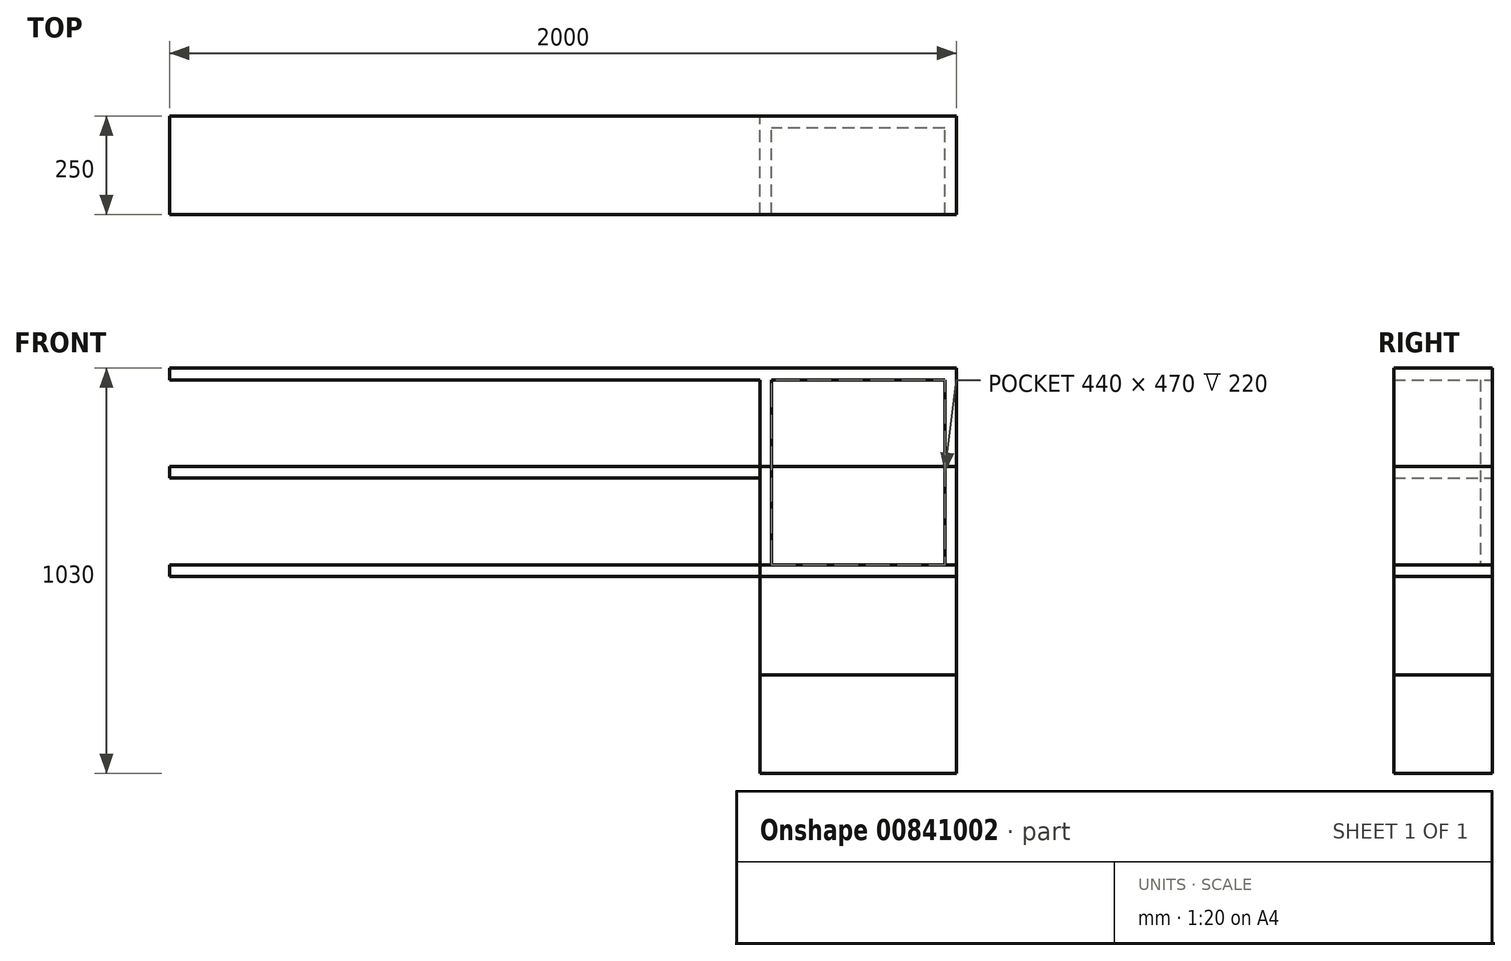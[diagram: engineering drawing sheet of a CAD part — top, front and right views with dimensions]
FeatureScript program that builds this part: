
annotation { "Feature Type Name" : "Feature", "Feature Type Description" : "" }
export const myFeature = defineFeature(function(context is Context, id is Id, definition is map)
    precondition{}
    {
        {
            var Q0;
            Q0=qCreatedBy(makeId("Top.planeOp"),FACE);
            var sketch = newSketch(context, id + "F0", { "sketchPlane" : qUnion([Q0])});
            skLineSegment(sketch, "E0.bottom", {"start": v(750, -125) * mm, "end": v(-750, -125) * mm});
            skLineSegment(sketch, "E0.top", {"start": v(750, 125) * mm, "end": v(-750, 125) * mm});
            skLineSegment(sketch, "E0.left", {"start": v(750, -125) * mm, "end": v(750, 125) * mm});
            skLineSegment(sketch, "E0.right", {"start": v(-750, -125) * mm, "end": v(-750, 125) * mm});
            skPoint(sketch, "E0.middle", {"position": v(0, 0) * mm});
            skSolve(sketch);
        }
        {
            var Q0;
            Q0=qSketchRegion(id+"F0",true);
            extrude(context, id + "F1", {"entities" : qUnion([Q0]), "depth" : 30 * mm, "offsetDistance" : 25 * mm});
        }
        {
            var Q0;
            Q0=makeQuery(id+"F1.opExtrude","SWEPT_FACE",FACE,{"disambiguationData":[OSD([sQuery(id+"F0.wireOp",EDGE,"E0.left")])]});
            extrude(context, id + "F2", {"entities" : qUnion([Q0]), "depth" : 500 * mm, "offsetDistance" : 25 * mm});
        }
        {
            var Q0;
            {var subQ0=sQuery(id+"F0.wireOp",EDGE,"E0.left");Q0=makeQuery(id+"F2.opExtrude","SWEPT_FACE",FACE,{"disambiguationData":[OSD([subQ0]),TDD([makeQuery(id+"F1.opExtrude","CAP_EDGE",EDGE,{"disambiguationData":[OSD([subQ0])],"isStart":true})])]});}
            extrude(context, id + "F3", {"entities" : qUnion([Q0]), "operationType" : NewBodyOperationType.ADD, "depth" : 500 * mm, "offsetDistance" : 25 * mm});
        }
        {
            var Q0;
            Q0=makeQuery(id+"F1.opExtrude","SWEPT_BODY",BODY,{"disambiguationData":[OSD([sQuery(id+"F0.wireOp",EDGE,"E0.bottom"),sQuery(id+"F0.wireOp",EDGE,"E0.top"),sQuery(id+"F0.wireOp",EDGE,"E0.left"),sQuery(id+"F0.wireOp",EDGE,"E0.right")])]});
            transform(context, id + "F4", {"entities" : qUnion([Q0]), "transformType" : TransformType.TRANSLATION_3D, "dx" : 0 * mm, "dy" : 0 * mm, "dz" : 0 * mm, "makeCopy" : true});
        }
        {
            var Q0;
            {var subQ0=sQuery(id+"F0.wireOp",EDGE,"E0.left");var subQ1=sQuery(id+"F0.wireOp",EDGE,"E0.bottom");Q0=makeQuery(id+"F3.boolean.opBoolean","MERGE",FACE,{"derivedFrom":[makeQuery(id+"F2.opExtrude","SWEPT_FACE",FACE,{"disambiguationData":[OSD([subQ1,subQ0])]}),makeQuery(id+"F3.opExtrude","SWEPT_FACE",FACE,{"disambiguationData":[OSD([subQ1,subQ0])]})]});}
            shell(context, id + "F5", {"entities" : qUnion([Q0]), "thickness" : 30 * mm});
        }
        {
            var Q0;
            Q0=makeQuery(id+"F4.opPattern","COPY",BODY,{"derivedFrom":makeQuery(id+"F1.opExtrude","SWEPT_BODY",BODY,{"disambiguationData":[OSD([sQuery(id+"F0.wireOp",EDGE,"E0.bottom"),sQuery(id+"F0.wireOp",EDGE,"E0.top"),sQuery(id+"F0.wireOp",EDGE,"E0.left"),sQuery(id+"F0.wireOp",EDGE,"E0.right")])]}),"instanceName":"1"});
            transform(context, id + "F6", {"entities" : qUnion([Q0]), "transformType" : TransformType.TRANSLATION_3D, "dx" : 0 * mm, "dy" : 0 * mm, "dz" : -500 * mm, "makeCopy" : false});
        }
        {
            var Q0;
            Q0=makeQuery(id+"F4.opPattern","COPY",BODY,{"derivedFrom":makeQuery(id+"F1.opExtrude","SWEPT_BODY",BODY,{"disambiguationData":[OSD([sQuery(id+"F0.wireOp",EDGE,"E0.bottom"),sQuery(id+"F0.wireOp",EDGE,"E0.top"),sQuery(id+"F0.wireOp",EDGE,"E0.left"),sQuery(id+"F0.wireOp",EDGE,"E0.right")])]}),"instanceName":"1"});
            transform(context, id + "F7", {"entities" : qUnion([Q0]), "transformType" : TransformType.TRANSLATION_3D, "dx" : 0 * mm, "dy" : 0 * mm, "dz" : 250 * mm, "makeCopy" : true});
        }
    });
